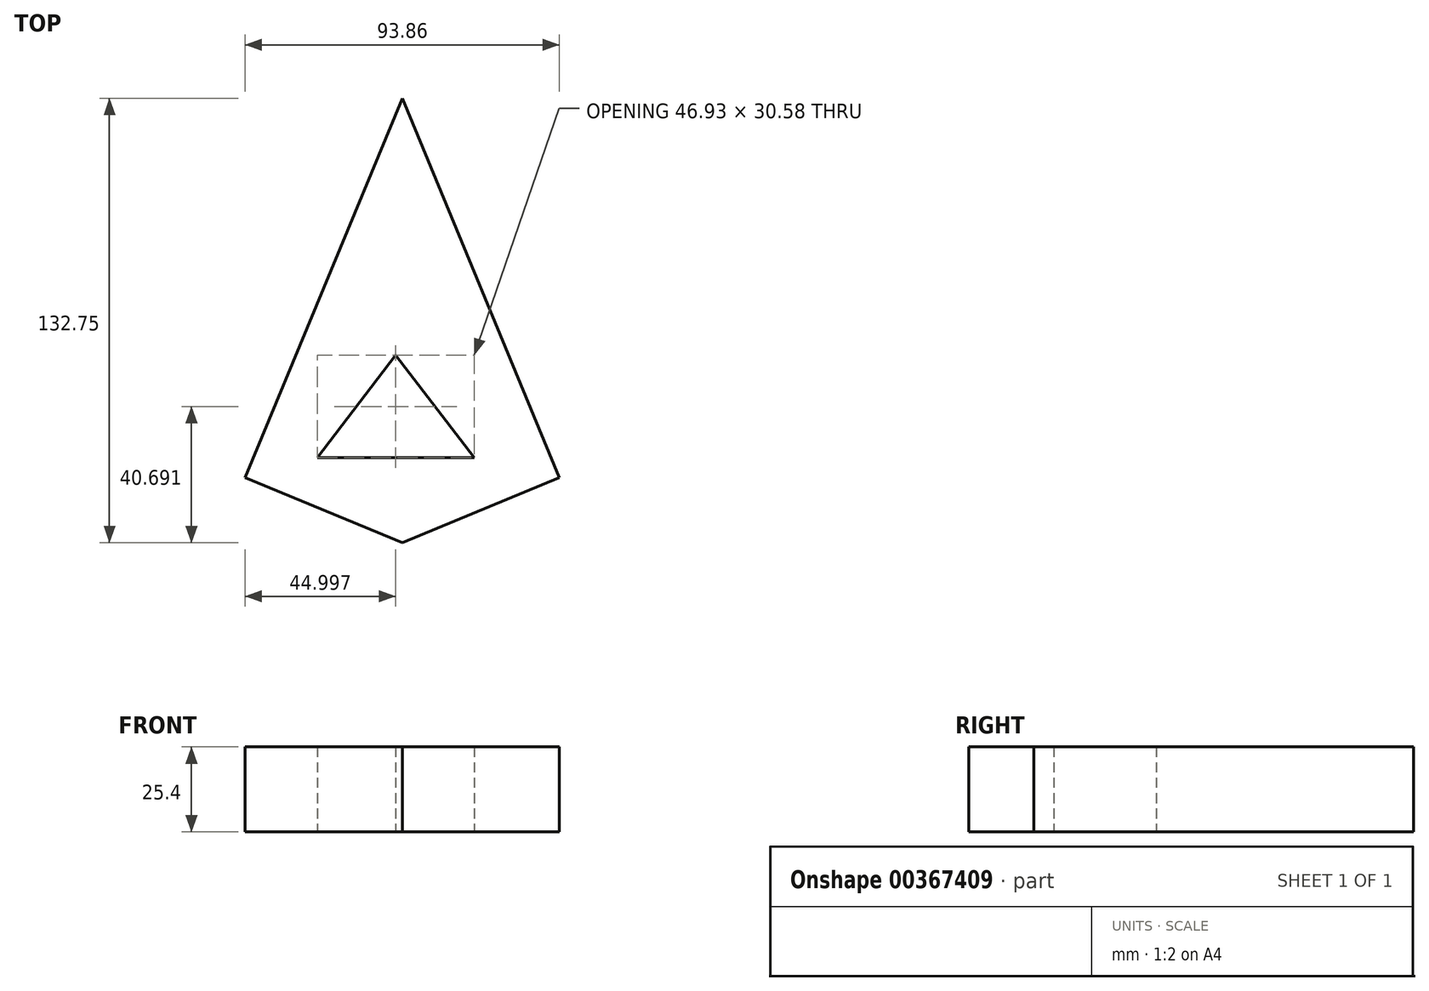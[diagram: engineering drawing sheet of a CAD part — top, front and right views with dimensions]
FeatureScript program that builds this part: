
annotation { "Feature Type Name" : "Feature", "Feature Type Description" : "" }
export const myFeature = defineFeature(function(context is Context, id is Id, definition is map)
    precondition{}
    {
        {
            var Q0;
            Q0=qCreatedBy(makeId("Top.planeOp"),FACE);
            var sketch = newSketch(context, id + "F0", { "sketchPlane" : qUnion([Q0])});
            skLineSegment(sketch, "E0", {"start": v(0, -19.44) * mm, "end": v(46.93, 0) * mm});
            skLineSegment(sketch, "E1", {"start": v(46.93, 0) * mm, "end": v(0, 113.3) * mm});
            skLineSegment(sketch, "E2", {"start": v(0, 113.3) * mm, "end": v(-46.93, 0) * mm});
            skLineSegment(sketch, "E3", {"start": v(-46.93, 0) * mm, "end": v(0, -19.44) * mm});
            skLineSegment(sketch, "E4", {"start": v(-25.4, 5.96) * mm, "end": v(-1.93, 36.54) * mm});
            skLineSegment(sketch, "E5", {"start": v(-1.93, 36.54) * mm, "end": v(21.53, 5.96) * mm});
            skLineSegment(sketch, "E6", {"start": v(21.53, 5.96) * mm, "end": v(-25.4, 5.96) * mm});
            skSolve(sketch);
        }
        {
            var Q0;
            Q0=makeQuery(id+"F0.imprint","IMPRINT",FACE,{"disambiguationData":[TD([[makeQuery(id+"F0.imprint","IMPRINT",EDGE,{"derivedFrom":sQuery(id+"F0.wireOp",EDGE,"E0")}),1.0]])]});
            extrude(context, id + "F1", {"entities" : qUnion([Q0]), "depth" : 25.4 * mm});
        }
    });
